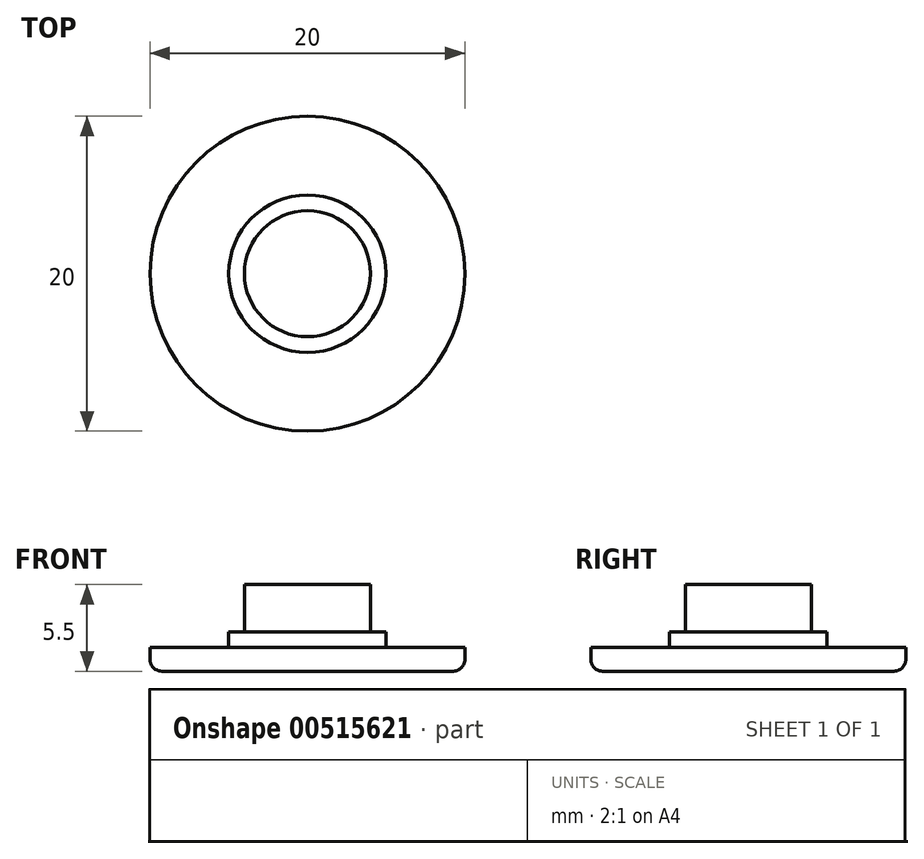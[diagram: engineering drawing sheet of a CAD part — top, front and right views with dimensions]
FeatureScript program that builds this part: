
annotation { "Feature Type Name" : "Feature", "Feature Type Description" : "" }
export const myFeature = defineFeature(function(context is Context, id is Id, definition is map)
    precondition{}
    {
        {
            var Q0;
            Q0=qCreatedBy(makeId("Top.planeOp"),FACE);
            var sketch = newSketch(context, id + "F0", { "sketchPlane" : qUnion([Q0])});
            skCircle(sketch, "E0", {"center": v(0, 0) * mm, "radius": 10 * mm});
            skSolve(sketch);
        }
        {
            var Q0;
            Q0=makeQuery(id+"F0.imprint","IMPRINT",FACE,{"disambiguationData":[TD([[makeQuery(id+"F0.imprint","IMPRINT",EDGE,{"derivedFrom":sQuery(id+"F0.wireOp",EDGE,"E0")}),1.0]])]});
            extrude(context, id + "F1", {"entities" : qUnion([Q0]), "depth" : 1.5 * mm, "offsetDistance" : 25 * mm});
        }
        {
            var Q0;
            Q0=makeQuery(id+"F1.opExtrude","CAP_FACE",FACE,{"disambiguationData":[OSD([sQuery(id+"F0.wireOp",EDGE,"E0")])],"isStart":false});
            var sketch = newSketch(context, id + "F2", { "sketchPlane" : qUnion([Q0])});
            skCircle(sketch, "E1", {"center": v(0, 0) * mm, "radius": 5 * mm});
            skSolve(sketch);
        }
        {
            var Q0;
            Q0=makeQuery(id+"F2.imprint","IMPRINT",FACE,{"disambiguationData":[TD([[makeQuery(id+"F2.imprint","IMPRINT",EDGE,{"derivedFrom":sQuery(id+"F2.wireOp",EDGE,"E1")}),1.0]])]});
            extrude(context, id + "F3", {"entities" : qUnion([Q0]), "operationType" : NewBodyOperationType.ADD, "depth" : 1 * mm, "offsetDistance" : 25 * mm});
        }
        {
            var Q0;
            Q0=makeQuery(id+"F3.opExtrude","CAP_FACE",FACE,{"disambiguationData":[OSD([sQuery(id+"F2.wireOp",EDGE,"E1")])],"isStart":false});
            var sketch = newSketch(context, id + "F4", { "sketchPlane" : qUnion([Q0])});
            skCircle(sketch, "E2", {"center": v(0, 0) * mm, "radius": 4 * mm});
            skSolve(sketch);
        }
        {
            var Q0;
            Q0=makeQuery(id+"F4.imprint","IMPRINT",FACE,{"disambiguationData":[TD([[makeQuery(id+"F4.imprint","IMPRINT",EDGE,{"derivedFrom":sQuery(id+"F4.wireOp",EDGE,"E2")}),1.0]])]});
            extrude(context, id + "F5", {"entities" : qUnion([Q0]), "operationType" : NewBodyOperationType.ADD, "depth" : 3 * mm, "offsetDistance" : 25 * mm});
        }
        {
            var Q0;
            Q0=makeQuery(id+"F1.opExtrude","CAP_EDGE",EDGE,{"disambiguationData":[OSD([sQuery(id+"F0.wireOp",EDGE,"E0")])],"isStart":true});
            fillet(context, id + "F6", {"entities" : qUnion([Q0]), "radius" : .75 * mm, "tangentPropagation" : true, "allowEdgeOverflow" : false});
        }
    });
